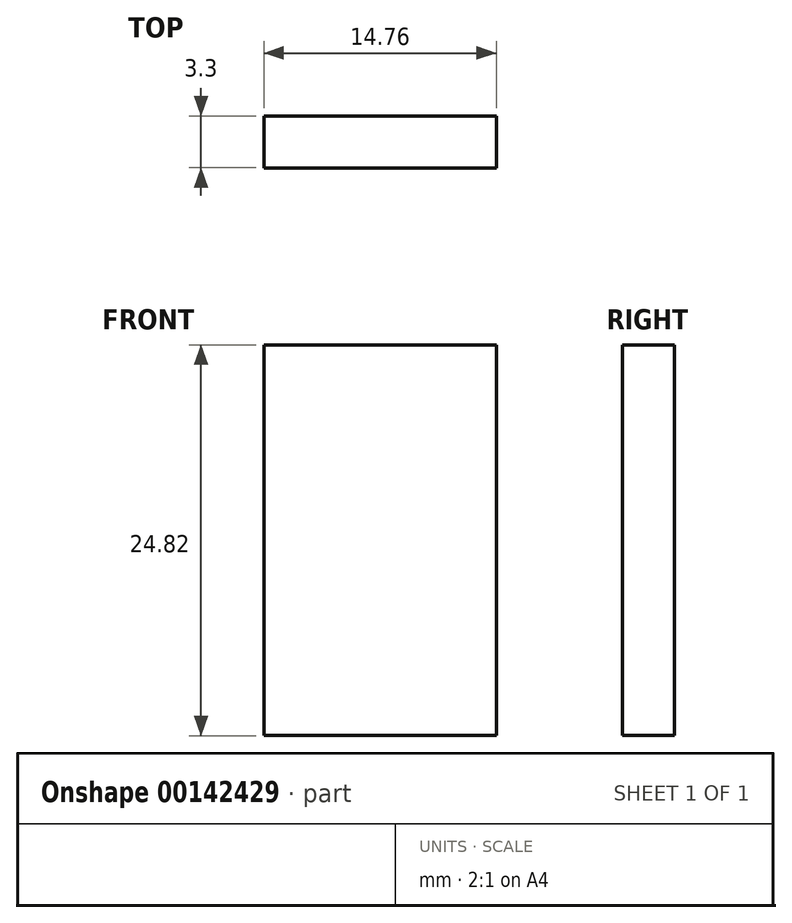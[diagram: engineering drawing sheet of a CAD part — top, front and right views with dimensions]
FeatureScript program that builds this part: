
annotation { "Feature Type Name" : "Feature", "Feature Type Description" : "" }
export const myFeature = defineFeature(function(context is Context, id is Id, definition is map)
    precondition{}
    {
        {
            var Q0;
            Q0=qCreatedBy(makeId("Front.planeOp"),FACE);
            var sketch = newSketch(context, id + "F0", { "sketchPlane" : qUnion([Q0])});
            skLineSegment(sketch, "E0.bottom", {"start": v(7.38, -12.4) * mm, "end": v(-7.38, -12.4) * mm});
            skLineSegment(sketch, "E0.top", {"start": v(7.38, 12.4) * mm, "end": v(-7.38, 12.4) * mm});
            skLineSegment(sketch, "E0.left", {"start": v(7.38, -12.4) * mm, "end": v(7.38, 12.4) * mm});
            skLineSegment(sketch, "E0.right", {"start": v(-7.38, -12.4) * mm, "end": v(-7.38, 12.4) * mm});
            skPoint(sketch, "E0.middle", {"position": v(0, 0) * mm});
            skSolve(sketch);
        }
        {
            var Q0;
            Q0 = qSketchRegion(id + "F0", true);
            extrude(context, id + "F1", {"entities" : qUnion([Q0]), "endBound" : BoundingType.SYMMETRIC, "depth" : 3.3 * mm});
        }
    });
